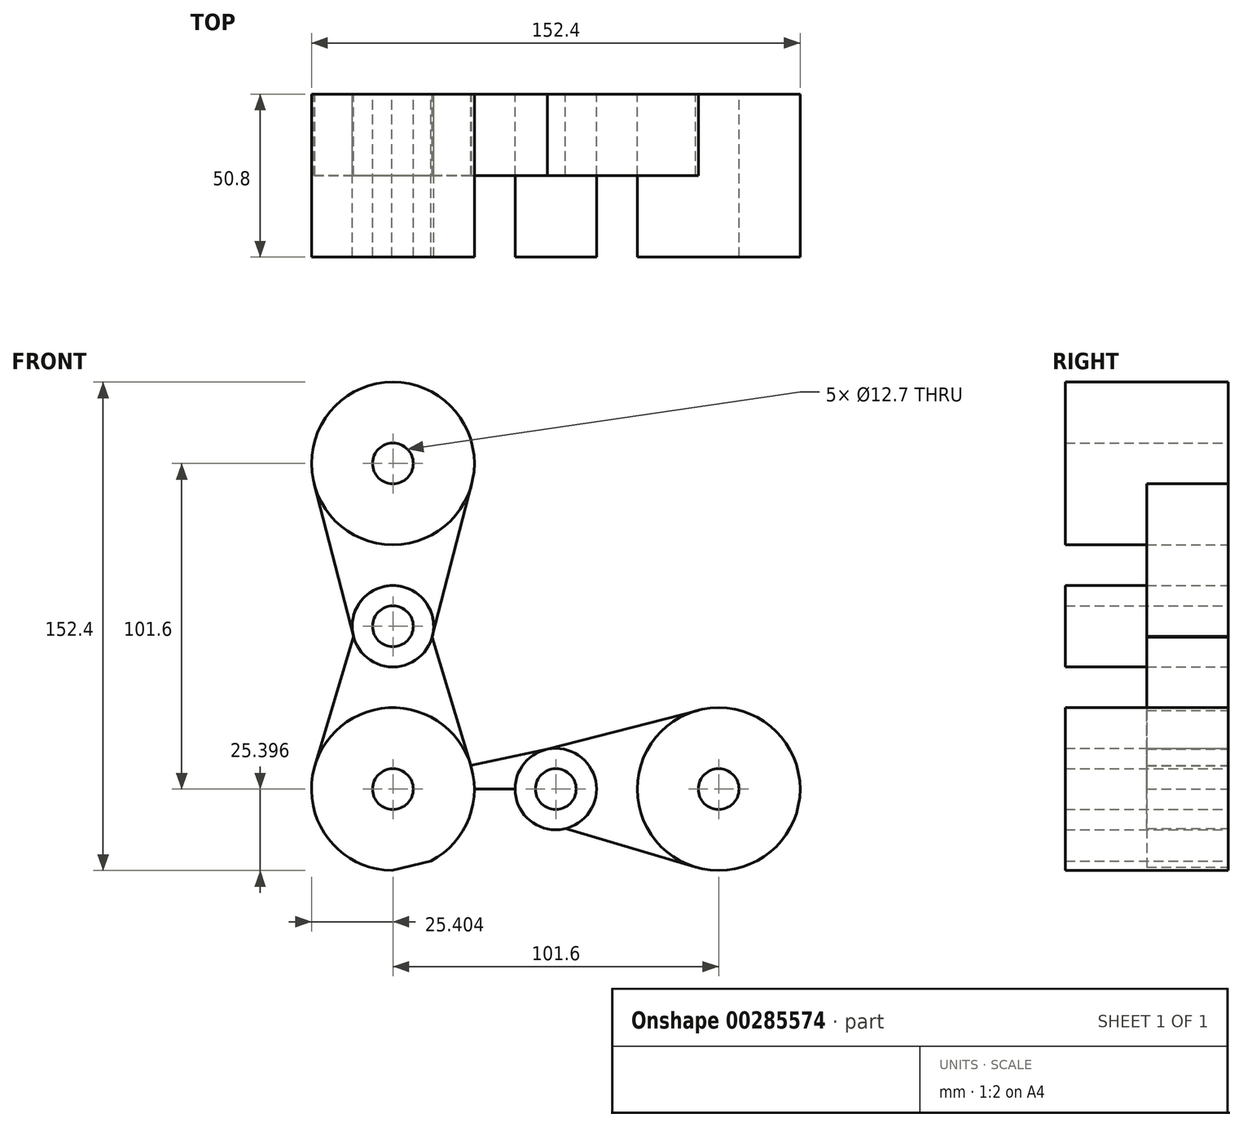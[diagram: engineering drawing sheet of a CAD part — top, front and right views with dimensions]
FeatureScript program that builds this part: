
annotation { "Feature Type Name" : "Feature", "Feature Type Description" : "" }
export const myFeature = defineFeature(function(context is Context, id is Id, definition is map)
    precondition{}
    {
        {
            var Q0;
            Q0=qCreatedBy(makeId("Front.planeOp"),FACE);
            var sketch = newSketch(context, id + "F0", { "sketchPlane" : qUnion([Q0])});
            skLineSegment(sketch, "E0", {"start": v(-42.1, -47.37) * mm, "end": v(8.7, -47.37) * mm});
            skLineSegment(sketch, "E1", {"start": v(-92.9, -47.37) * mm, "end": v(-92.9, 3.43) * mm});
            skLineSegment(sketch, "E2", {"start": v(-92.9, 3.43) * mm, "end": v(-92.9, 54.23) * mm});
            skCircle(sketch, "E3", {"center": v(-92.9, 54.23) * mm, "radius": 25.4 * mm});
            skCircle(sketch, "E4", {"center": v(-92.9, -47.37) * mm, "radius": 25.4 * mm});
            skCircle(sketch, "E5", {"center": v(8.7, -47.37) * mm, "radius": 25.4 * mm});
            skCircle(sketch, "E6", {"center": v(-92.9, 3.43) * mm, "radius": 12.7 * mm});
            skCircle(sketch, "E7", {"center": v(-42.1, -47.37) * mm, "radius": 12.7 * mm});
            skLineSegment(sketch, "E8", {"start": v(-92.9, -47.37) * mm, "end": v(-42.1, -47.37) * mm});
            skLineSegment(sketch, "E9", {"start": v(-117.5, 47.88) * mm, "end": v(-105.2, 0.25) * mm});
            skLineSegment(sketch, "E10", {"start": v(-105.2, 0.25) * mm, "end": v(-117.25, -40.11) * mm});
            skLineSegment(sketch, "E11", {"start": v(-68.31, 47.88) * mm, "end": v(-80.67, 0) * mm});
            skLineSegment(sketch, "E12", {"start": v(-80.67, 0) * mm, "end": v(-68.6, -40.03) * mm});
            skLineSegment(sketch, "E13", {"start": v(-68.6, -40.03) * mm, "end": v(-44.75, -34.95) * mm});
            skLineSegment(sketch, "E14", {"start": v(-44.75, -34.95) * mm, "end": v(2.34, -22.78) * mm});
            skLineSegment(sketch, "E15", {"start": v(-93.24, -72.77) * mm, "end": v(-39.13, -59.72) * mm});
            skLineSegment(sketch, "E16", {"start": v(-39.13, -59.72) * mm, "end": v(1.5, -71.73) * mm});
            skSolve(sketch);
        }
        {
            var Q0;
            {var subQ0=sQuery(id+"F0.wireOp",EDGE,"E3");var subQ1=makeQuery(id+"F0.imprint","INTERSECT",VERTEX,{"derivedFrom":[subQ0,sQuery(id+"F0.wireOp",EDGE,"E9")]});Q0=makeQuery(id+"F0.imprint","IMPRINT",FACE,{"disambiguationData":[TD([[makeQuery(id+"F0.imprint","IMPRINT",EDGE,{"disambiguationData":[TD([[subQ1,-1.0]])],"derivedFrom":subQ0}),1.0]])]});}
            var Q1;
            {var subQ0=sQuery(id+"F0.wireOp",EDGE,"E2");var subQ1=sQuery(id+"F0.wireOp",EDGE,"E1");var subQ2=makeQuery(id+"F0.imprint","INTERSECT",VERTEX,{"derivedFrom":[subQ1,subQ0]});Q1=makeQuery(id+"F0.imprint","IMPRINT",FACE,{"disambiguationData":[TD([[makeQuery(id+"F0.imprint","IMPRINT",EDGE,{"disambiguationData":[TD([[subQ2,1.0]])],"derivedFrom":subQ1}),-1.0]])]});}
            var Q2;
            {var subQ0=sQuery(id+"F0.wireOp",EDGE,"E2");var subQ1=sQuery(id+"F0.wireOp",EDGE,"E1");var subQ2=makeQuery(id+"F0.imprint","INTERSECT",VERTEX,{"derivedFrom":[subQ1,subQ0]});Q2=makeQuery(id+"F0.imprint","IMPRINT",FACE,{"disambiguationData":[TD([[makeQuery(id+"F0.imprint","IMPRINT",EDGE,{"disambiguationData":[TD([[subQ2,1.0]])],"derivedFrom":subQ1}),1.0]])]});}
            var Q3;
            {var subQ3=sQuery(id+"F0.wireOp",EDGE,"E8");var subQ7=sQuery(id+"F0.wireOp",EDGE,"E1");var subQ8=makeQuery(id+"F0.imprint","INTERSECT",VERTEX,{"derivedFrom":[subQ7,subQ3]});Q3=makeQuery(id+"F0.imprint","IMPRINT",FACE,{"disambiguationData":[TD([[makeQuery(id+"F0.imprint","IMPRINT",EDGE,{"disambiguationData":[TD([[subQ8,-1.0]])],"derivedFrom":subQ7}),1.0]])]});}
            var Q4;
            {var subQ0=sQuery(id+"F0.wireOp",EDGE,"E5");var subQ1=makeQuery(id+"F0.imprint","INTERSECT",VERTEX,{"derivedFrom":[subQ0,sQuery(id+"F0.wireOp",EDGE,"E14")]});Q4=makeQuery(id+"F0.imprint","IMPRINT",FACE,{"disambiguationData":[TD([[makeQuery(id+"F0.imprint","IMPRINT",EDGE,{"disambiguationData":[TD([[subQ1,-1.0]])],"derivedFrom":subQ0}),1.0]])]});}
            var Q5;
            {var subQ0=sQuery(id+"F0.wireOp",EDGE,"E8");var subQ1=sQuery(id+"F0.wireOp",EDGE,"E1");var subQ2=makeQuery(id+"F0.imprint","INTERSECT",VERTEX,{"derivedFrom":[subQ1,subQ0]});Q5=makeQuery(id+"F0.imprint","IMPRINT",FACE,{"disambiguationData":[TD([[makeQuery(id+"F0.imprint","IMPRINT",EDGE,{"disambiguationData":[TD([[subQ2,-1.0]])],"derivedFrom":subQ1}),-1.0]])]});}
            var Q6;
            {var subQ0=sQuery(id+"F0.wireOp",EDGE,"E8");var subQ1=sQuery(id+"F0.wireOp",EDGE,"E0");var subQ2=makeQuery(id+"F0.imprint","INTERSECT",VERTEX,{"derivedFrom":[subQ1,subQ0]});Q6=makeQuery(id+"F0.imprint","IMPRINT",FACE,{"disambiguationData":[TD([[makeQuery(id+"F0.imprint","IMPRINT",EDGE,{"disambiguationData":[TD([[subQ2,-1.0]])],"derivedFrom":subQ1}),1.0]])]});}
            var Q7;
            {var subQ0=sQuery(id+"F0.wireOp",EDGE,"E8");var subQ1=sQuery(id+"F0.wireOp",EDGE,"E0");var subQ2=makeQuery(id+"F0.imprint","INTERSECT",VERTEX,{"derivedFrom":[subQ1,subQ0]});Q7=makeQuery(id+"F0.imprint","IMPRINT",FACE,{"disambiguationData":[TD([[makeQuery(id+"F0.imprint","IMPRINT",EDGE,{"disambiguationData":[TD([[subQ2,-1.0]])],"derivedFrom":subQ1}),-1.0]])]});}
            extrude(context, id + "F1", {"entities" : qUnion([Q0, Q1, Q2, Q3, Q4, Q5, Q6, Q7]), "depth" : 50.8 * mm});
        }
        {
            var Q0;
            {var subQ5=sQuery(id+"F0.wireOp",EDGE,"E9");Q0=makeQuery(id+"F0.imprint","IMPRINT",FACE,{"disambiguationData":[TD([[makeQuery(id+"F0.imprint","IMPRINT",EDGE,{"derivedFrom":subQ5}),1.0]])]});}
            var Q1;
            {var subQ0=sQuery(id+"F0.wireOp",EDGE,"E3");var subQ1=sQuery(id+"F0.wireOp",EDGE,"E2");var subQ2=makeQuery(id+"F0.imprint","INTERSECT",VERTEX,{"derivedFrom":[subQ1,subQ0]});Q1=makeQuery(id+"F0.imprint","IMPRINT",FACE,{"disambiguationData":[TD([[makeQuery(id+"F0.imprint","IMPRINT",EDGE,{"disambiguationData":[TD([[subQ2,1.0]])],"derivedFrom":subQ1}),-1.0]])]});}
            var Q2;
            {var subQ5=sQuery(id+"F0.wireOp",EDGE,"E10");Q2=makeQuery(id+"F0.imprint","IMPRINT",FACE,{"disambiguationData":[TD([[makeQuery(id+"F0.imprint","IMPRINT",EDGE,{"derivedFrom":subQ5}),1.0]])]});}
            var Q3;
            {var subQ5=sQuery(id+"F0.wireOp",EDGE,"E12");Q3=makeQuery(id+"F0.imprint","IMPRINT",FACE,{"disambiguationData":[TD([[makeQuery(id+"F0.imprint","IMPRINT",EDGE,{"derivedFrom":subQ5}),-1.0]])]});}
            var Q4;
            {var subQ5=sQuery(id+"F0.wireOp",EDGE,"E14");Q4=makeQuery(id+"F0.imprint","IMPRINT",FACE,{"disambiguationData":[TD([[makeQuery(id+"F0.imprint","IMPRINT",EDGE,{"derivedFrom":subQ5}),-1.0]])]});}
            var Q5;
            {var subQ5=sQuery(id+"F0.wireOp",EDGE,"E16");Q5=makeQuery(id+"F0.imprint","IMPRINT",FACE,{"disambiguationData":[TD([[makeQuery(id+"F0.imprint","IMPRINT",EDGE,{"derivedFrom":subQ5}),1.0]])]});}
            var Q6;
            {var subQ0=sQuery(id+"F0.wireOp",EDGE,"E15");var subQ1=sQuery(id+"F0.wireOp",EDGE,"E4");var subQ2=makeQuery(id+"F0.imprint","INTERSECT",VERTEX,{"disambiguationData":[OD(1.0)],"derivedFrom":[subQ1,subQ0]});Q6=makeQuery(id+"F0.imprint","IMPRINT",FACE,{"disambiguationData":[TD([[makeQuery(id+"F0.imprint","IMPRINT",EDGE,{"disambiguationData":[TD([[subQ2,-1.0]])],"derivedFrom":subQ1}),-1.0]])]});}
            var Q7;
            {var subQ0=sQuery(id+"F0.wireOp",EDGE,"E13");Q7=makeQuery(id+"F0.imprint","IMPRINT",FACE,{"disambiguationData":[TD([[makeQuery(id+"F0.imprint","IMPRINT",EDGE,{"derivedFrom":subQ0}),-1.0]])]});}
            extrude(context, id + "F2", {"entities" : qUnion([Q0, Q1, Q2, Q3, Q4, Q5, Q6, Q7]), "depth" : 25.4 * mm});
        }
        {
            var Q0;
            Q0=sQuery(id+"F0.wireOp",VERTEX,"E1.start");
            var Q1;
            Q1=sQuery(id+"F0.wireOp",VERTEX,"E6.center");
            var Q2;
            Q2=sQuery(id+"F0.wireOp",VERTEX,"E2.end");
            var Q3;
            Q3=sQuery(id+"F0.wireOp",VERTEX,"E7.center");
            var Q4;
            Q4=sQuery(id+"F0.wireOp",VERTEX,"E0.end");
            var Q5;
            Q5=makeQuery(id+"F1.opExtrude","SWEPT_BODY",BODY,{"disambiguationData":[OSD([sQuery(id+"F0.wireOp",EDGE,"E4"),sQuery(id+"F0.wireOp",EDGE,"E15")])]});
            var Q6;
            Q6=makeQuery(id+"F1.opExtrude","SWEPT_BODY",BODY,{"disambiguationData":[OSD([sQuery(id+"F0.wireOp",EDGE,"E6")])]});
            var Q7;
            Q7=makeQuery(id+"F1.opExtrude","SWEPT_BODY",BODY,{"disambiguationData":[OSD([sQuery(id+"F0.wireOp",EDGE,"E3")])]});
            var Q8;
            Q8=makeQuery(id+"F1.opExtrude","SWEPT_BODY",BODY,{"disambiguationData":[OSD([sQuery(id+"F0.wireOp",EDGE,"E7")])]});
            var Q9;
            Q9=makeQuery(id+"F1.opExtrude","SWEPT_BODY",BODY,{"disambiguationData":[OSD([sQuery(id+"F0.wireOp",EDGE,"E5")])]});
            hole(context, id + "F3", {"style" : HoleStyle.SIMPLE, "endStyle" : HoleEndStyle.THROUGH, "oppositeDirection" : true, "holeDiameter" : 12.7 * mm, "tappedDepth" : 12.7 * mm, "tapClearance" : 3, "locations" : qUnion([Q0, Q1, Q2, Q3, Q4]), "scope" : qUnion([Q5, Q6, Q7, Q8, Q9])});
        }
    });
